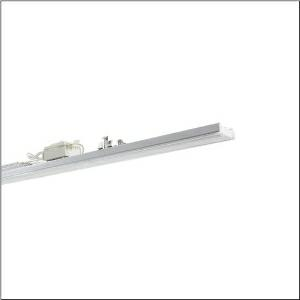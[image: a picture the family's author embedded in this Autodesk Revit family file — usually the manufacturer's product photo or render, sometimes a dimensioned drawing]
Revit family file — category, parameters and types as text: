
# Revit family: licross_r__21_recessed_mo_52tl12dn5axg_ab9b
name_source: partatom
category: Lighting Fixtures
units: mm (PartAtom-declared; Revit-internal decimal feet)

## family parameters
Cut with Voids When Loaded = No
Host = Face
Light Source = No
Part Type = Normal
Room Calculation Point = No
Round Connector Dimension = Use Diameter
Shared = No

## types (1)
- --- (1 x LED, 10170 lm, 58 W, 5000K)
    Apparent Load = 58 VA
    CIE Flux Codes = 72 92 99 100 100
    Color Rendering = 80
    Color Temperature = 5000K
    Default Elevation = 1800 mm
    Description = Licross® 21 Recessed MO, luminaire insert, of sheet steel, galvanised, coil coated, white, length: 1.500mm, width: 66mm, height: 67mm, LED rated luminous flux: 10.180lm, light colour: 850, control gear: DALI 2, with plug, 5-pole, with phase selection, mains connection: 220..240V, AC, 50/60Hz, rated input power: 58W, internal wiring halogen-free, primary optical cover: cover, of PMMA, light emission: direct distribution, primary light characteristic: symmetric, protection rating (complete): IP40, insulation class (complete): insulation class I (protective earthing), certification: CE, ENEC, VDE, UKCA, protection symbol: D if used in an environment without relevant dust loads with corresponding accessories, impact resistance: IK06, permissible ambient temperature for indoor applications: -25..+35°C, corresponds to IFS (International Featured Standards) requirements for safety and quality in the food industry, reducing of maximum allowable ambient temperature of 5°C with ceiling mounting, LABS conformity tested according to VDMA 24364:2018-05, packaging unit: 1 piece
    Height = 58 mm
    Lamp = 1 x LED
    Lamp Light Flux = 10170 lm
    Lamp Power = 58 W
    Lamp count = 1
    Length = 1500 mm
    Luminous efficacy = 175 lm/W
    Manufacturer = Siteco
    ModVariant = No
    Model = 52TL12DN5AXG
    Mounting Place = Ceiling
    Mounting Type = Pendant
    Number of Poles = 1
    OnlyDefault = Yes
    Power Factor = 1
    Product Name = Licross® 21 Recessed MO
    Product group = luminaire insert | ceiling pendant
    ProductGroupID = 902
    Protection Class = Protection class I
    Protection Degree = IP 40
    RLX_Detail_Level = 1
    RLX_Emergency_Light_Flux = 0 lm
    RLX_Emergency_Type = 0
    RLX_Emergency_Type_DB = No
    RlxData = <blob elided: 24593 chars, md5=fc148b11>
    Socket = socket
    Standby Power = 0 W
    System Light Flux = 10170 lm
    System Power = 58 W
    Type Comments = factory setting: luminous flux: 100 % | dim-lin: 254 | 390 mA
    Type Image = l_1296930.jpg
    URL = http://relux.com
    VarID = @adj_111127
    Voltage = 0 V
    Weight = 0.00 kg
    Width = 66 mm

## geometry (parser evidence)
native form markers: Blend x4, Sweep x13
no freeform markers — native parametric forms only
